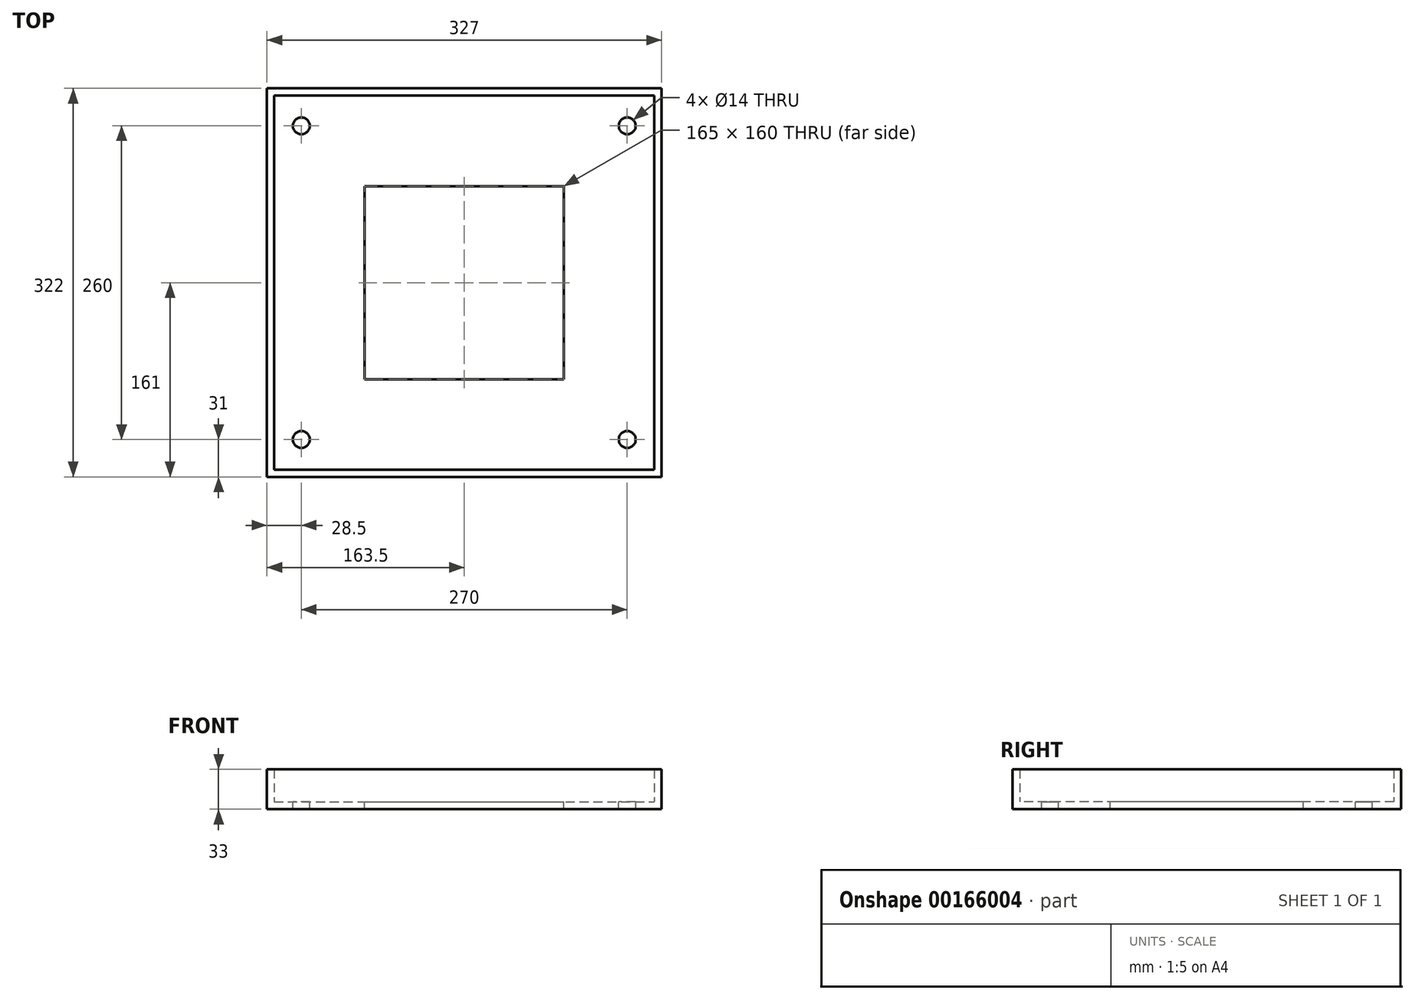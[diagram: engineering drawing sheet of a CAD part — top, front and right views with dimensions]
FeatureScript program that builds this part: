
annotation { "Feature Type Name" : "Feature", "Feature Type Description" : "" }
export const myFeature = defineFeature(function(context is Context, id is Id, definition is map)
    precondition{}
    {
        {
            var Q0;
            Q0=qCreatedBy(makeId("Top.planeOp"),FACE);
            var sketch = newSketch(context, id + "F0", { "sketchPlane" : qUnion([Q0])});
            skLineSegment(sketch, "E0.bottom", {"start": v(-163.5, 161) * mm, "end": v(163.5, 161) * mm});
            skLineSegment(sketch, "E0.top", {"start": v(-163.5, -161) * mm, "end": v(163.5, -161) * mm});
            skLineSegment(sketch, "E0.left", {"start": v(-163.5, 161) * mm, "end": v(-163.5, -161) * mm});
            skLineSegment(sketch, "E0.right", {"start": v(163.5, 161) * mm, "end": v(163.5, -161) * mm});
            skSolve(sketch);
        }
        {
            var Q0;
            Q0=makeQuery(id+"F0.imprint","IMPRINT",FACE,{"disambiguationData":[TD([[makeQuery(id+"F0.imprint","IMPRINT",EDGE,{"derivedFrom":sQuery(id+"F0.wireOp",EDGE,"E0.bottom")}),-1.0]])]});
            extrude(context, id + "F1", {"entities" : qUnion([Q0]), "endBound" : BoundingType.SYMMETRIC, "depth" : 33 * mm});
        }
        {
            var Q0;
            Q0=makeQuery(id+"F1.opExtrude","CAP_FACE",FACE,{"disambiguationData":[OSD([sQuery(id+"F0.wireOp",EDGE,"E0.bottom"),sQuery(id+"F0.wireOp",EDGE,"E0.top"),sQuery(id+"F0.wireOp",EDGE,"E0.left"),sQuery(id+"F0.wireOp",EDGE,"E0.right")])],"isStart":false});
            shell(context, id + "F2", {"entities" : qUnion([Q0]), "thickness" : 6 * mm});
        }
        {
            var Q0;
            Q0=qCreatedBy(makeId("Top.planeOp"),FACE);
            var sketch = newSketch(context, id + "F3", { "sketchPlane" : qUnion([Q0])});
            skLineSegment(sketch, "E1.bottom", {"start": v(-82.5, 80) * mm, "end": v(82.5, 80) * mm});
            skLineSegment(sketch, "E1.top", {"start": v(-82.5, -80) * mm, "end": v(82.5, -80) * mm});
            skLineSegment(sketch, "E1.left", {"start": v(-82.5, 80) * mm, "end": v(-82.5, -80) * mm});
            skLineSegment(sketch, "E1.right", {"start": v(82.5, 80) * mm, "end": v(82.5, -80) * mm});
            skSolve(sketch);
        }
        {
            var Q0;
            Q0 = qSketchRegion(id + "F3", true);
            extrude(context, id + "F4", {"entities" : qUnion([Q0]), "operationType" : NewBodyOperationType.REMOVE, "endBound" : BoundingType.THROUGH_ALL, "oppositeDirection" : true, "depth" : 25 * mm});
        }
        {
            var Q0;
            Q0=makeQuery(id+"F2.opShell","OFFSET_FACE",FACE,{"disambiguationData":[OSD([sQuery(id+"F0.wireOp",EDGE,"E0.bottom"),sQuery(id+"F0.wireOp",EDGE,"E0.top"),sQuery(id+"F0.wireOp",EDGE,"E0.left"),sQuery(id+"F0.wireOp",EDGE,"E0.right")])]});
            var sketch = newSketch(context, id + "F5", { "sketchPlane" : qUnion([Q0])});
            skPoint(sketch, "E2", {"position": v(-135, 130) * mm});
            skPoint(sketch, "E3", {"position": v(135, 130) * mm});
            skPoint(sketch, "E4", {"position": v(135, -130) * mm});
            skPoint(sketch, "E5", {"position": v(-135, -130) * mm});
            skSolve(sketch);
        }
        {
            var Q0;
            Q0=sQuery(id+"F5.wireOp",VERTEX,"E2");
            var Q1;
            Q1=sQuery(id+"F5.wireOp",VERTEX,"E3");
            var Q2;
            Q2=sQuery(id+"F5.wireOp",VERTEX,"E4");
            var Q3;
            Q3=sQuery(id+"F5.wireOp",VERTEX,"E5");
            var Q4;
            Q4=makeQuery(id+"F1.opExtrude","SWEPT_BODY",BODY,{"disambiguationData":[OSD([sQuery(id+"F0.wireOp",EDGE,"E0.bottom"),sQuery(id+"F0.wireOp",EDGE,"E0.top"),sQuery(id+"F0.wireOp",EDGE,"E0.left"),sQuery(id+"F0.wireOp",EDGE,"E0.right")])]});
            hole(context, id + "F6", {"style" : HoleStyle.SIMPLE, "endStyle" : HoleEndStyle.THROUGH, "holeDiameter" : 14 * mm, "locations" : qUnion([Q0, Q1, Q2, Q3]), "scope" : qUnion([Q4]), "isTappedThrough" : true});
        }
    });
